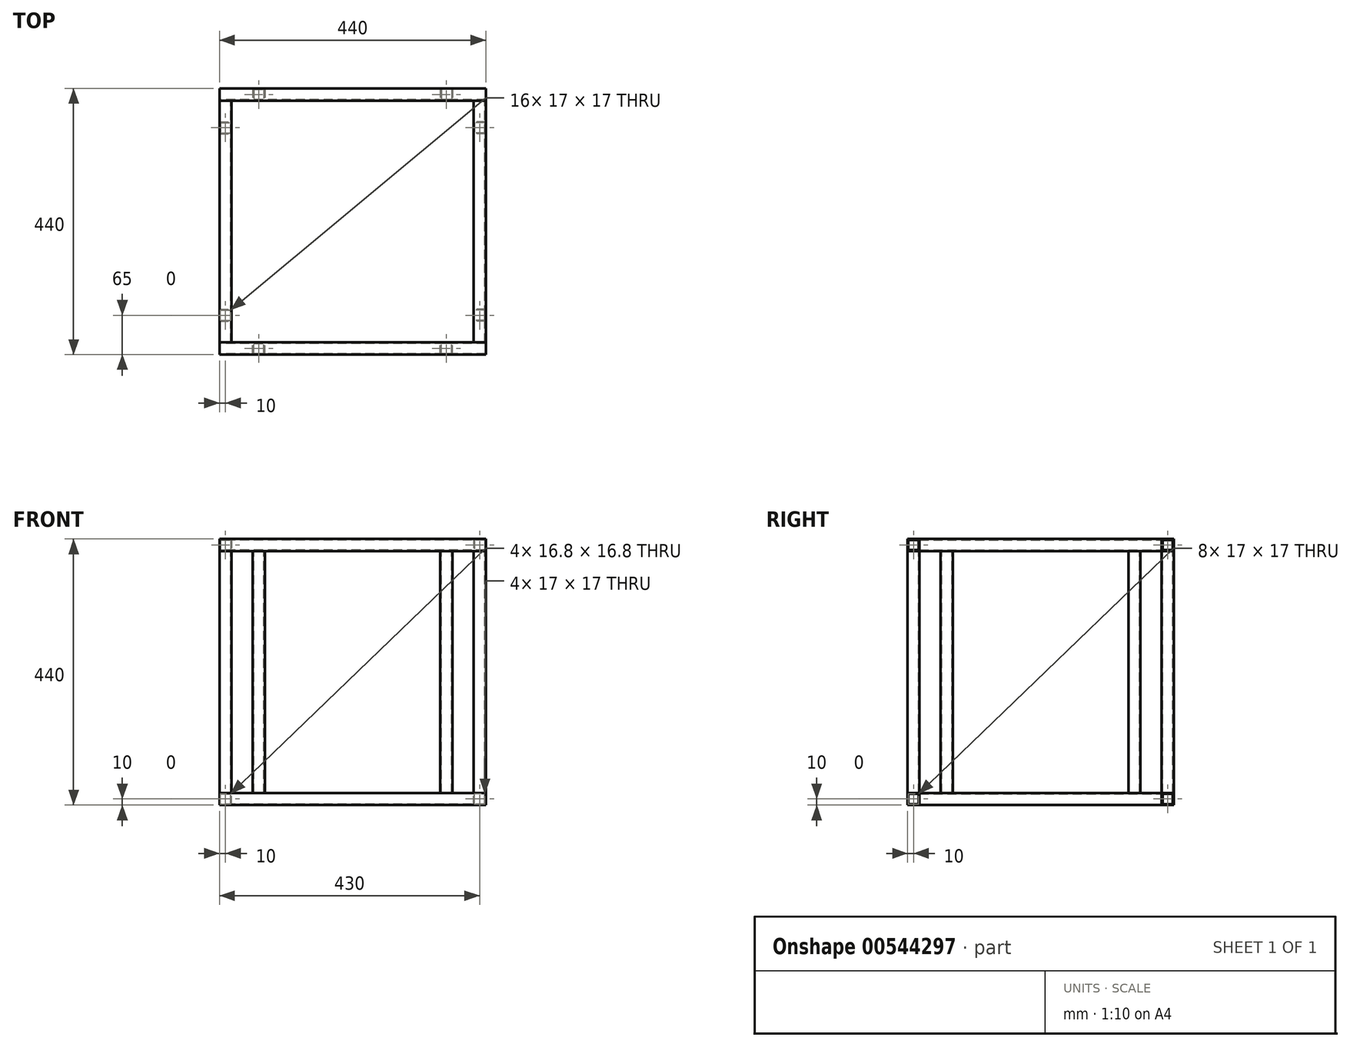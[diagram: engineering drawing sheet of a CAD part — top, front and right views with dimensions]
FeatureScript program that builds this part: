
annotation { "Feature Type Name" : "Feature", "Feature Type Description" : "" }
export const myFeature = defineFeature(function(context is Context, id is Id, definition is map)
    precondition{}
    {
        {
            var Q0;
            Q0=qCreatedBy(makeId("Front.planeOp"),FACE);
            var sketch = newSketch(context, id + "F0", { "sketchPlane" : qUnion([Q0])});
            skLineSegment(sketch, "E0.bottom", {"start": v(-220, 10) * mm, "end": v(-200, 10) * mm});
            skLineSegment(sketch, "E0.top", {"start": v(-220, -10) * mm, "end": v(-200, -10) * mm});
            skLineSegment(sketch, "E0.left", {"start": v(-220, 10) * mm, "end": v(-220, -10) * mm});
            skLineSegment(sketch, "E0.right", {"start": v(-200, 10) * mm, "end": v(-200, -10) * mm});
            skPoint(sketch, "E0.middle", {"position": v(-210, 0) * mm});
            skLineSegment(sketch, "E1.MirrorCS", {"start": v(220, 10) * mm, "end": v(200, 10) * mm});
            skPoint(sketch, "E2.MirrorP", {"position": v(210, 0) * mm});
            skLineSegment(sketch, "E3.MirrorCS", {"start": v(200, 10) * mm, "end": v(200, -10) * mm});
            skLineSegment(sketch, "E4.MirrorCS", {"start": v(220, 10) * mm, "end": v(220, -10) * mm});
            skLineSegment(sketch, "E5.MirrorCS", {"start": v(220, -10) * mm, "end": v(200, -10) * mm});
            skLineSegment(sketch, "E6.0", {"start": v(-218.4, 8.4) * mm, "end": v(-201.6, 8.4) * mm});
            skLineSegment(sketch, "E6.1", {"start": v(-218.4, 8.4) * mm, "end": v(-218.4, -8.4) * mm});
            skLineSegment(sketch, "E6.2", {"start": v(-218.4, -8.4) * mm, "end": v(-201.6, -8.4) * mm});
            skLineSegment(sketch, "E6.3", {"start": v(-201.6, 8.4) * mm, "end": v(-201.6, -8.4) * mm});
            skLineSegment(sketch, "E7.0", {"start": v(218.5, 8.5) * mm, "end": v(201.5, 8.5) * mm});
            skLineSegment(sketch, "E7.1", {"start": v(218.5, 8.5) * mm, "end": v(218.5, -8.5) * mm});
            skLineSegment(sketch, "E7.2", {"start": v(218.5, -8.5) * mm, "end": v(201.5, -8.5) * mm});
            skLineSegment(sketch, "E7.3", {"start": v(201.5, 8.5) * mm, "end": v(201.5, -8.5) * mm});
            skSolve(sketch);
        }
        {
            var Q0;
            Q0=makeQuery(id+"F0.imprint","IMPRINT",FACE,{"disambiguationData":[TD([[makeQuery(id+"F0.imprint","IMPRINT",EDGE,{"derivedFrom":sQuery(id+"F0.wireOp",EDGE,"E0.bottom")}),-1.0]])]});
            var Q1;
            Q1=makeQuery(id+"F0.imprint","IMPRINT",FACE,{"disambiguationData":[TD([[makeQuery(id+"F0.imprint","IMPRINT",EDGE,{"derivedFrom":sQuery(id+"F0.wireOp",EDGE,"E1.MirrorCS")}),1.0]])]});
            extrude(context, id + "F1", {"entities" : qUnion([Q0, Q1]), "endBound" : BoundingType.SYMMETRIC, "depth" : 400 * mm, "offsetDistance" : 25 * mm});
        }
        {
            var Q0;
            Q0=makeQuery(id+"F1.opExtrude","CAP_EDGE",EDGE,{"disambiguationData":[OSD([sQuery(id+"F0.wireOp",EDGE,"E0.left")])],"isStart":false});
            cPlane(context, id + "F2", {"entities" : qUnion([Q0]), "cplaneType" : CPlaneType.LINE_ANGLE, "offset" : 25 * mm, "angle" : 0 * degree, "width" : 150 * mm, "height" : 150 * mm});
        }
        {
            var Q0;
            Q0=qCreatedBy(id+"F2.planeOp",FACE);
            var sketch = newSketch(context, id + "F3", { "sketchPlane" : qUnion([Q0])});
            skLineSegment(sketch, "E8.0", {"start": v(200, 10) * mm, "end": v(200, -10) * mm});
            skLineSegment(sketch, "E9.bottom", {"start": v(200, 10) * mm, "end": v(220, 10) * mm});
            skLineSegment(sketch, "E9.top", {"start": v(200, -10) * mm, "end": v(220, -10) * mm});
            skLineSegment(sketch, "E9.right", {"start": v(220, 10) * mm, "end": v(220, -10) * mm});
            skLineSegment(sketch, "E10.0", {"start": v(201.5, 8.5) * mm, "end": v(201.5, -8.5) * mm});
            skLineSegment(sketch, "E10.1", {"start": v(201.5, 8.5) * mm, "end": v(218.5, 8.5) * mm});
            skLineSegment(sketch, "E10.2", {"start": v(218.5, 8.5) * mm, "end": v(218.5, -8.5) * mm});
            skLineSegment(sketch, "E10.3", {"start": v(201.5, -8.5) * mm, "end": v(218.5, -8.5) * mm});
            skLineSegment(sketch, "E11.MirrorCS", {"start": v(-200, 10) * mm, "end": v(-200, -10) * mm});
            skLineSegment(sketch, "E12.MirrorCS", {"start": v(-200, 10) * mm, "end": v(-220, 10) * mm});
            skLineSegment(sketch, "E13.MirrorCS", {"start": v(-200, -10) * mm, "end": v(-220, -10) * mm});
            skLineSegment(sketch, "E14.MirrorCS", {"start": v(-220, 10) * mm, "end": v(-220, -10) * mm});
            skLineSegment(sketch, "E15.MirrorCS", {"start": v(-201.5, 8.5) * mm, "end": v(-201.5, -8.5) * mm});
            skLineSegment(sketch, "E16.MirrorCS", {"start": v(-201.5, 8.5) * mm, "end": v(-218.5, 8.5) * mm});
            skLineSegment(sketch, "E17.MirrorCS", {"start": v(-201.5, -8.5) * mm, "end": v(-218.5, -8.5) * mm});
            skLineSegment(sketch, "E18.MirrorCS", {"start": v(-218.5, 8.5) * mm, "end": v(-218.5, -8.5) * mm});
            skSolve(sketch);
        }
        {
            var Q0;
            Q0=makeQuery(id+"F3.imprint","IMPRINT",FACE,{"disambiguationData":[TD([[makeQuery(id+"F3.imprint","IMPRINT",EDGE,{"derivedFrom":sQuery(id+"F3.wireOp",EDGE,"E12.MirrorCS")}),1.0]])]});
            var Q1;
            Q1=makeQuery(id+"F3.imprint","IMPRINT",FACE,{"disambiguationData":[TD([[makeQuery(id+"F3.imprint","IMPRINT",EDGE,{"derivedFrom":sQuery(id+"F3.wireOp",EDGE,"E9.bottom")}),-1.0]])]});
            var Q2;
            Q2=makeQuery(id+"F1.opExtrude","SWEPT_FACE",FACE,{"disambiguationData":[OSD([sQuery(id+"F0.wireOp",EDGE,"E4.MirrorCS")])]});
            extrude(context, id + "F4", {"entities" : qUnion([Q0, Q1]), "endBound" : BoundingType.UP_TO_SURFACE, "oppositeDirection" : true, "depth" : 25 * mm, "endBoundEntityFace" : qUnion([Q2]), "offsetDistance" : 25 * mm});
        }
        {
            var Q0;
            Q0=makeQuery(id+"F4.opExtrude","SWEPT_FACE",FACE,{"disambiguationData":[OSD([sQuery(id+"F3.wireOp",EDGE,"E9.top")])]});
            var sketch = newSketch(context, id + "F5", { "sketchPlane" : qUnion([Q0])});
            skLineSegment(sketch, "E19.bottom", {"start": v(-165, 220) * mm, "end": v(-145, 220) * mm});
            skLineSegment(sketch, "E19.top", {"start": v(-165, 200) * mm, "end": v(-145, 200) * mm});
            skLineSegment(sketch, "E19.left", {"start": v(-165, 220) * mm, "end": v(-165, 200) * mm});
            skLineSegment(sketch, "E19.right", {"start": v(-145, 220) * mm, "end": v(-145, 200) * mm});
            skLineSegment(sketch, "E20.0", {"start": v(-163.5, 218.5) * mm, "end": v(-146.5, 218.5) * mm});
            skLineSegment(sketch, "E20.1", {"start": v(-163.5, 218.5) * mm, "end": v(-163.5, 201.5) * mm});
            skLineSegment(sketch, "E20.2", {"start": v(-163.5, 201.5) * mm, "end": v(-146.5, 201.5) * mm});
            skLineSegment(sketch, "E20.3", {"start": v(-146.5, 218.5) * mm, "end": v(-146.5, 201.5) * mm});
            skLineSegment(sketch, "E21.MirrorCS", {"start": v(165, 220) * mm, "end": v(145, 220) * mm});
            skLineSegment(sketch, "E22.MirrorCS", {"start": v(163.5, 218.5) * mm, "end": v(146.5, 218.5) * mm});
            skLineSegment(sketch, "E23.MirrorCS", {"start": v(146.5, 218.5) * mm, "end": v(146.5, 201.5) * mm});
            skLineSegment(sketch, "E24.MirrorCS", {"start": v(163.5, 201.5) * mm, "end": v(146.5, 201.5) * mm});
            skLineSegment(sketch, "E25.MirrorCS", {"start": v(163.5, 218.5) * mm, "end": v(163.5, 201.5) * mm});
            skLineSegment(sketch, "E26.MirrorCS", {"start": v(165, 220) * mm, "end": v(165, 200) * mm});
            skLineSegment(sketch, "E27.MirrorCS", {"start": v(165, 200) * mm, "end": v(145, 200) * mm});
            skLineSegment(sketch, "E28.MirrorCS", {"start": v(145, 220) * mm, "end": v(145, 200) * mm});
            skLineSegment(sketch, "E29.MirrorCS", {"start": v(-165, -220) * mm, "end": v(-145, -220) * mm});
            skLineSegment(sketch, "E30.MirrorCS", {"start": v(-163.5, -218.5) * mm, "end": v(-146.5, -218.5) * mm});
            skLineSegment(sketch, "E31.MirrorCS", {"start": v(-146.5, -218.5) * mm, "end": v(-146.5, -201.5) * mm});
            skLineSegment(sketch, "E32.MirrorCS", {"start": v(-145, -220) * mm, "end": v(-145, -200) * mm});
            skLineSegment(sketch, "E33.MirrorCS", {"start": v(-163.5, -218.5) * mm, "end": v(-163.5, -201.5) * mm});
            skLineSegment(sketch, "E34.MirrorCS", {"start": v(-163.5, -201.5) * mm, "end": v(-146.5, -201.5) * mm});
            skLineSegment(sketch, "E35.MirrorCS", {"start": v(-165, -200) * mm, "end": v(-145, -200) * mm});
            skLineSegment(sketch, "E36.MirrorCS", {"start": v(-165, -220) * mm, "end": v(-165, -200) * mm});
            skLineSegment(sketch, "E37.MirrorCS", {"start": v(163.5, -218.5) * mm, "end": v(163.5, -201.5) * mm});
            skLineSegment(sketch, "E38.MirrorCS", {"start": v(163.5, -201.5) * mm, "end": v(146.5, -201.5) * mm});
            skLineSegment(sketch, "E39.MirrorCS", {"start": v(146.5, -218.5) * mm, "end": v(146.5, -201.5) * mm});
            skLineSegment(sketch, "E40.MirrorCS", {"start": v(163.5, -218.5) * mm, "end": v(146.5, -218.5) * mm});
            skLineSegment(sketch, "E41.MirrorCS", {"start": v(165, -220) * mm, "end": v(145, -220) * mm});
            skLineSegment(sketch, "E42.MirrorCS", {"start": v(145, -220) * mm, "end": v(145, -200) * mm});
            skLineSegment(sketch, "E43.MirrorCS", {"start": v(165, -200) * mm, "end": v(145, -200) * mm});
            skLineSegment(sketch, "E44.MirrorCS", {"start": v(165, -220) * mm, "end": v(165, -200) * mm});
            skLineSegment(sketch, "E45.0", {"start": v(-220, 200) * mm, "end": v(-220, -200) * mm, "construction": true});
            skLineSegment(sketch, "E46.0", {"start": v(-200, 200) * mm, "end": v(-200, -200) * mm, "construction": true});
            skLineSegment(sketch, "E47.bottom", {"start": v(-220, 165) * mm, "end": v(-200, 165) * mm});
            skLineSegment(sketch, "E47.top", {"start": v(-220, 145) * mm, "end": v(-200, 145) * mm});
            skLineSegment(sketch, "E47.left", {"start": v(-220, 165) * mm, "end": v(-220, 145) * mm});
            skLineSegment(sketch, "E47.right", {"start": v(-200, 165) * mm, "end": v(-200, 145) * mm});
            skLineSegment(sketch, "E48.0", {"start": v(-218.5, 163.5) * mm, "end": v(-218.5, 146.5) * mm});
            skLineSegment(sketch, "E48.1", {"start": v(-218.5, 163.5) * mm, "end": v(-201.5, 163.5) * mm});
            skLineSegment(sketch, "E48.2", {"start": v(-201.5, 163.5) * mm, "end": v(-201.5, 146.5) * mm});
            skLineSegment(sketch, "E48.3", {"start": v(-218.5, 146.5) * mm, "end": v(-201.5, 146.5) * mm});
            skLineSegment(sketch, "E49.MirrorCS", {"start": v(220, 165) * mm, "end": v(220, 145) * mm});
            skLineSegment(sketch, "E50.MirrorCS", {"start": v(218.5, 163.5) * mm, "end": v(218.5, 146.5) * mm});
            skLineSegment(sketch, "E51.MirrorCS", {"start": v(220, 145) * mm, "end": v(200, 145) * mm});
            skLineSegment(sketch, "E52.MirrorCS", {"start": v(220, 165) * mm, "end": v(200, 165) * mm});
            skLineSegment(sketch, "E53.MirrorCS", {"start": v(200, 165) * mm, "end": v(200, 145) * mm});
            skLineSegment(sketch, "E54.MirrorCS", {"start": v(201.5, 163.5) * mm, "end": v(201.5, 146.5) * mm});
            skLineSegment(sketch, "E55.MirrorCS", {"start": v(218.5, 146.5) * mm, "end": v(201.5, 146.5) * mm});
            skLineSegment(sketch, "E56.MirrorCS", {"start": v(218.5, 163.5) * mm, "end": v(201.5, 163.5) * mm});
            skLineSegment(sketch, "E57.MirrorCS", {"start": v(-220, -165) * mm, "end": v(-220, -145) * mm});
            skLineSegment(sketch, "E58.MirrorCS", {"start": v(-218.5, -163.5) * mm, "end": v(-218.5, -146.5) * mm});
            skLineSegment(sketch, "E59.MirrorCS", {"start": v(-220, -145) * mm, "end": v(-200, -145) * mm});
            skLineSegment(sketch, "E60.MirrorCS", {"start": v(-218.5, -163.5) * mm, "end": v(-201.5, -163.5) * mm});
            skLineSegment(sketch, "E61.MirrorCS", {"start": v(-201.5, -163.5) * mm, "end": v(-201.5, -146.5) * mm});
            skLineSegment(sketch, "E62.MirrorCS", {"start": v(-200, -165) * mm, "end": v(-200, -145) * mm});
            skLineSegment(sketch, "E63.MirrorCS", {"start": v(-218.5, -146.5) * mm, "end": v(-201.5, -146.5) * mm});
            skLineSegment(sketch, "E64.MirrorCS", {"start": v(-220, -165) * mm, "end": v(-200, -165) * mm});
            skLineSegment(sketch, "E65.MirrorCS", {"start": v(220, -165) * mm, "end": v(200, -165) * mm});
            skLineSegment(sketch, "E66.MirrorCS", {"start": v(218.5, -146.5) * mm, "end": v(201.5, -146.5) * mm});
            skLineSegment(sketch, "E67.MirrorCS", {"start": v(220, -145) * mm, "end": v(200, -145) * mm});
            skLineSegment(sketch, "E68.MirrorCS", {"start": v(220, -165) * mm, "end": v(220, -145) * mm});
            skLineSegment(sketch, "E69.MirrorCS", {"start": v(218.5, -163.5) * mm, "end": v(218.5, -146.5) * mm});
            skLineSegment(sketch, "E70.MirrorCS", {"start": v(201.5, -163.5) * mm, "end": v(201.5, -146.5) * mm});
            skLineSegment(sketch, "E71.MirrorCS", {"start": v(200, -165) * mm, "end": v(200, -145) * mm});
            skLineSegment(sketch, "E72.MirrorCS", {"start": v(218.5, -163.5) * mm, "end": v(201.5, -163.5) * mm});
            skSolve(sketch);
        }
        {
            var Q0;
            Q0=makeQuery(id+"F5.imprint","IMPRINT",FACE,{"disambiguationData":[TD([[makeQuery(id+"F5.imprint","IMPRINT",EDGE,{"derivedFrom":sQuery(id+"F5.wireOp",EDGE,"E19.bottom")}),1.0]])]});
            var Q1;
            Q1=makeQuery(id+"F5.imprint","IMPRINT",FACE,{"disambiguationData":[TD([[makeQuery(id+"F5.imprint","IMPRINT",EDGE,{"derivedFrom":sQuery(id+"F5.wireOp",EDGE,"E21.MirrorCS")}),1.0]])]});
            var Q2;
            Q2=makeQuery(id+"F5.imprint","IMPRINT",FACE,{"disambiguationData":[TD([[makeQuery(id+"F5.imprint","IMPRINT",EDGE,{"derivedFrom":sQuery(id+"F5.wireOp",EDGE,"E29.MirrorCS")}),1.0]])]});
            var Q3;
            Q3=makeQuery(id+"F5.imprint","IMPRINT",FACE,{"disambiguationData":[TD([[makeQuery(id+"F5.imprint","IMPRINT",EDGE,{"derivedFrom":sQuery(id+"F5.wireOp",EDGE,"E37.MirrorCS")}),-1.0]])]});
            var Q4;
            Q4=makeQuery(id+"F5.imprint","IMPRINT",FACE,{"disambiguationData":[TD([[makeQuery(id+"F5.imprint","IMPRINT",EDGE,{"derivedFrom":sQuery(id+"F5.wireOp",EDGE,"E47.bottom")}),-1.0]])]});
            var Q5;
            Q5=makeQuery(id+"F5.imprint","IMPRINT",FACE,{"disambiguationData":[TD([[makeQuery(id+"F5.imprint","IMPRINT",EDGE,{"derivedFrom":sQuery(id+"F5.wireOp",EDGE,"E57.MirrorCS")}),-1.0]])]});
            var Q6;
            Q6=makeQuery(id+"F5.imprint","IMPRINT",FACE,{"disambiguationData":[TD([[makeQuery(id+"F5.imprint","IMPRINT",EDGE,{"derivedFrom":sQuery(id+"F5.wireOp",EDGE,"E49.MirrorCS")}),-1.0]])]});
            var Q7;
            Q7=makeQuery(id+"F5.imprint","IMPRINT",FACE,{"disambiguationData":[TD([[makeQuery(id+"F5.imprint","IMPRINT",EDGE,{"derivedFrom":sQuery(id+"F5.wireOp",EDGE,"E65.MirrorCS")}),-1.0]])]});
            extrude(context, id + "F6", {"entities" : qUnion([Q0, Q1, Q2, Q3, Q4, Q5, Q6, Q7]), "depth" : 400 * mm, "offsetDistance" : 25 * mm});
        }
        {
            var Q0;
            Q0=makeQuery(id+"F6.opExtrude","CAP_VERTEX",VERTEX,{"disambiguationData":[OSD([sQuery(id+"F5.wireOp",EDGE,"E41.MirrorCS"),sQuery(id+"F5.wireOp",EDGE,"E44.MirrorCS")])],"isStart":true});
            var Q1;
            Q1=makeQuery(id+"F6.opExtrude","CAP_VERTEX",VERTEX,{"disambiguationData":[OSD([sQuery(id+"F5.wireOp",EDGE,"E41.MirrorCS"),sQuery(id+"F5.wireOp",EDGE,"E44.MirrorCS")])],"isStart":false});
            cPlane(context, id + "F7", {"entities" : qUnion([Q0, Q1]), "cplaneType" : CPlaneType.MID_PLANE, "offset" : 25 * mm, "width" : 150 * mm, "height" : 150 * mm});
        }
        {
            var Q0;
            Q0=makeQuery(id+"F4.opExtrude","SWEPT_BODY",BODY,{"disambiguationData":[OSD([sQuery(id+"F3.wireOp",EDGE,"E9.bottom"),sQuery(id+"F3.wireOp",EDGE,"E9.top"),sQuery(id+"F3.wireOp",EDGE,"E8.0"),sQuery(id+"F3.wireOp",EDGE,"E9.right"),sQuery(id+"F3.wireOp",EDGE,"E10.0"),sQuery(id+"F3.wireOp",EDGE,"E10.1"),sQuery(id+"F3.wireOp",EDGE,"E10.2"),sQuery(id+"F3.wireOp",EDGE,"E10.3")])]});
            var Q1;
            Q1=makeQuery(id+"F1.opExtrude","SWEPT_BODY",BODY,{"disambiguationData":[OSD([sQuery(id+"F0.wireOp",EDGE,"E1.MirrorCS"),sQuery(id+"F0.wireOp",EDGE,"E3.MirrorCS"),sQuery(id+"F0.wireOp",EDGE,"E4.MirrorCS"),sQuery(id+"F0.wireOp",EDGE,"E5.MirrorCS"),sQuery(id+"F0.wireOp",EDGE,"E7.0"),sQuery(id+"F0.wireOp",EDGE,"E7.1"),sQuery(id+"F0.wireOp",EDGE,"E7.2"),sQuery(id+"F0.wireOp",EDGE,"E7.3")])]});
            var Q2;
            Q2=makeQuery(id+"F1.opExtrude","SWEPT_BODY",BODY,{"disambiguationData":[OSD([sQuery(id+"F0.wireOp",EDGE,"E0.bottom"),sQuery(id+"F0.wireOp",EDGE,"E0.top"),sQuery(id+"F0.wireOp",EDGE,"E0.left"),sQuery(id+"F0.wireOp",EDGE,"E0.right"),sQuery(id+"F0.wireOp",EDGE,"E6.0"),sQuery(id+"F0.wireOp",EDGE,"E6.1"),sQuery(id+"F0.wireOp",EDGE,"E6.2"),sQuery(id+"F0.wireOp",EDGE,"E6.3")])]});
            var Q3;
            Q3=makeQuery(id+"F4.opExtrude","SWEPT_BODY",BODY,{"disambiguationData":[OSD([sQuery(id+"F3.wireOp",EDGE,"E12.MirrorCS"),sQuery(id+"F3.wireOp",EDGE,"E13.MirrorCS"),sQuery(id+"F3.wireOp",EDGE,"E11.MirrorCS"),sQuery(id+"F3.wireOp",EDGE,"E14.MirrorCS"),sQuery(id+"F3.wireOp",EDGE,"E15.MirrorCS"),sQuery(id+"F3.wireOp",EDGE,"E16.MirrorCS"),sQuery(id+"F3.wireOp",EDGE,"E17.MirrorCS"),sQuery(id+"F3.wireOp",EDGE,"E18.MirrorCS")])]});
            var Q4;
            Q4=qCreatedBy(id+"F7.planeOp",FACE);
            mirror(context, id + "F8", {"entities" : qUnion([Q0, Q1, Q2, Q3]), "mirrorPlane" : qUnion([Q4])});
        }
    });
